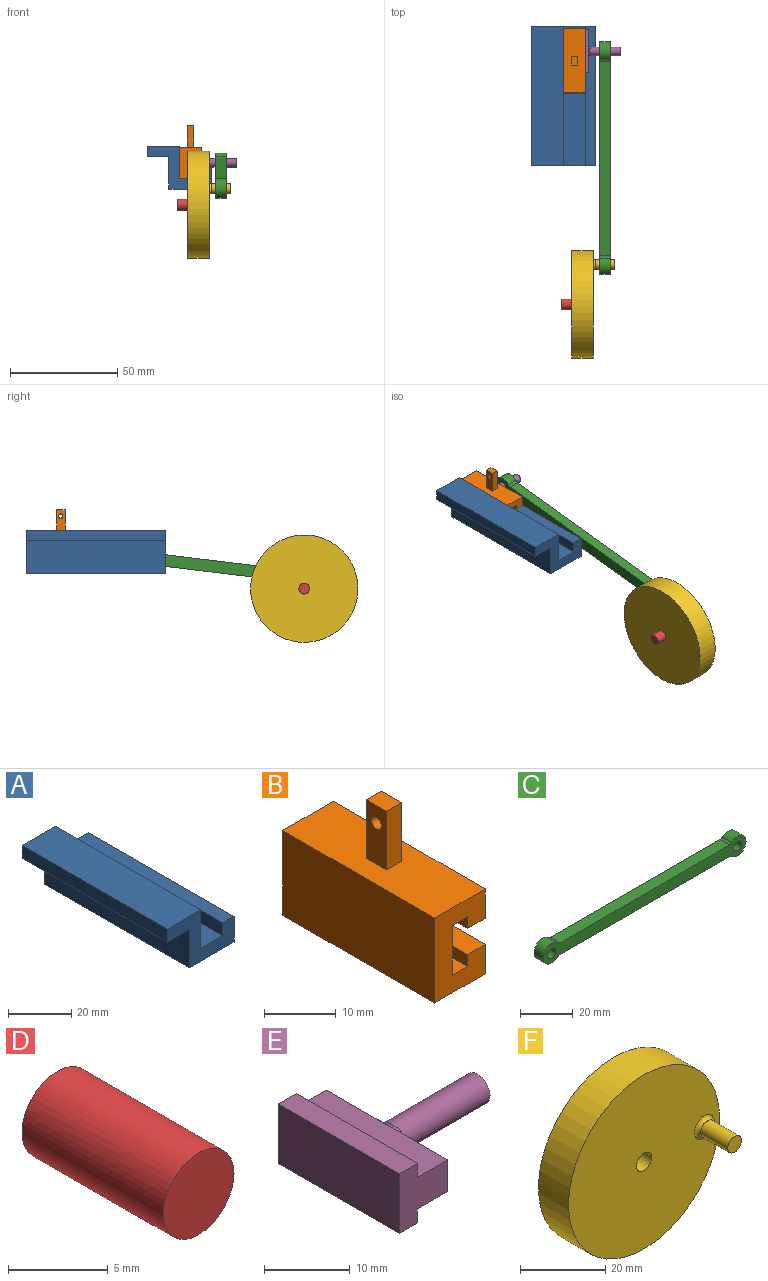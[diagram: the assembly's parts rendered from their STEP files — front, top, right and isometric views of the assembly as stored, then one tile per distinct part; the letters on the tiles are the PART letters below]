
ASSEMBLY  parts=6 mates=5
PART A: 12 faces, bbox 30x65x20 mm
  f0: plane 65x20mm, normal (0,0,-1), area 1300mm2, adj f1,f9,f10,f11
  f1: plane 65x10mm, normal (1,0,0), area 650mm2, adj f0,f2,f10,f11
  f2: plane 65x5mm, normal (0,0,1), area 325mm2, adj f1,f3,f10,f11
  f3: plane 65x5mm, normal (-1,0,0), area 325mm2, adj f2,f4,f10,f11
  f4: plane 65x10mm, normal (0,0,1), area 650mm2, adj f3,f5,f10,f11
  f5: plane 65x15mm, normal (1,0,0), area 975mm2, adj f4,f6,f10,f11
  f6: plane 65x15mm, normal (0,0,1), area 975mm2, adj f5,f7,f10,f11
  f7: plane 65x5mm, normal (-1,0,0), area 325mm2, adj f6,f8,f10,f11
  f8: plane 65x10mm, normal (0,0,-1), area 650mm2, adj f7,f9,f10,f11
  f9: plane 65x15mm, normal (-1,0,0), area 975mm2, adj f0,f8,f10,f11
  f10: plane 30x20mm, normal (0,-1,0), area 250mm2, adj f0,f1,f2,f3,f4,f5,f6,f7
  f11: plane 30x20mm, normal (0,1,0), area 250mm2, adj f0,f1,f2,f3,f4,f5,f6,f7
PART B: 20 faces, bbox 10x30x24.5 mm
  f0: plane 30x3mm, normal (0,0,1), area 90mm2, adj f1,f11,f12,f13
  f1: plane 30x8.5mm, normal (1,0,0), area 255mm2, adj f0,f2,f12,f13
  f2: plane 30x3mm, normal (0,0,-1), area 90mm2, adj f1,f3,f12,f13
  f3: plane 30x2mm, normal (-1,0,0), area 60mm2, adj f2,f4,f12,f13
  f4: plane 30x3.5mm, normal (0,0,-1), area 105mm2, adj f3,f5,f12,f13
  f5: plane 30x5mm, normal (1,0,0), area 150mm2, adj f4,f6,f12,f13
  f6: plane 30x10mm, normal (0,0,1), area 288mm2, adj f5,f7,f12,f13,f14,f15,f16,f17
  f7: plane 30x14.5mm, normal (-1,0,0), area 435mm2, adj f6,f8,f12,f13
  f8: plane 30x10mm, normal (0,0,-1), area 300mm2, adj f7,f9,f12,f13
  f9: plane 30x5mm, normal (1,0,0), area 150mm2, adj f8,f10,f12,f13
  f10: plane 30x3.5mm, normal (0,0,1), area 105mm2, adj f9,f11,f12,f13
  f11: plane 30x2mm, normal (-1,0,0), area 60mm2, adj f0,f10,f12,f13
  f12: plane 14.5x10mm, normal (0,-1,0), area 103.7mm2, adj f0,f1,f2,f3,f4,f5,f6,f7
  f13: plane 14.5x10mm, normal (0,1,0), area 103.8mm2, adj f0,f1,f2,f3,f4,f5,f6,f7
  f14: plane 10x3mm, normal (0,-1,0), area 30mm2, adj f6,f15,f17,f18
  f15: plane 10x4mm, normal (1,0,0), area 36.9mm2, adj f6,f14,f16,f18,f19
  f16: plane 10x3mm, normal (0,1,0), area 30mm2, adj f6,f15,f17,f18
  f17: plane 10x4mm, normal (-1,0,0), area 36.9mm2, adj f6,f14,f16,f18,f19
  f18: plane 4x3mm, normal (0,0,1), area 12mm2, adj f14,f15,f16,f17
  f19: cylinder r=1mm len=3mm, axis (-1,0,0), area 18.8mm2, adj f15,f17
PART C: 12 faces, bbox 109x5x9 mm
  f0: cylinder r=4.5mm len=9mm, axis (0,1,0), area 105mm2, adj f6,f7,f8,f9
  f1: plane 91.02x5mm, normal (0,0,-1), area 455.1mm2, adj f6,f7,f9,f10
  f2: cylinder r=4.5mm len=9mm, axis (0,1,0), area 105mm2, adj f6,f7,f10,f11
  f3: plane 91.02x5mm, normal (0,0,1), area 455.1mm2, adj f6,f7,f8,f11
  f4: cylinder r=2.25mm len=5mm, axis (0,1,0), area 70.7mm2, adj f6,f7
  f5: cylinder r=2mm len=5mm, axis (0,1,0), area 62.8mm2, adj f6,f7
  f6: plane 109x9mm, normal (0,-1,0), area 594mm2, adj f0,f1,f2,f3,f4,f5,f8,f9
  f7: plane 109x9mm, normal (0,1,0), area 594mm2, adj f0,f1,f2,f3,f4,f5,f8,f9
  f8: cylinder r=2mm len=5mm, axis (0,1,0), area 7.6mm2, adj f0,f3,f6,f7
  f9: cylinder r=2mm len=5mm, axis (0,1,0), area 7.6mm2, adj f0,f1,f6,f7
  f10: cylinder r=2mm len=5mm, axis (0,1,0), area 7.6mm2, adj f1,f2,f6,f7
  f11: cylinder r=2mm len=5mm, axis (0,1,0), area 7.6mm2, adj f2,f3,f6,f7
PART D: 3 faces, bbox 5x10x5 mm
  f0: cylinder r=2.5mm len=10mm, axis (0,1,0), area 157.1mm2, adj f1,f2
  f1: plane 5x5mm, normal (0,-1,0), area 19.6mm2, adj f0
  f2: plane 5x5mm, normal (0,1,0), area 19.6mm2, adj f0
PART E: 17 faces, bbox 23.1x20.1x8.6 mm
  f0: plane 8.02x4.5mm, normal (1,0,0), area 32.9mm2, adj f1,f3,f9,f14
  f1: plane 20.14x5.14mm, normal (0,0,-1), area 100mm2, adj f0,f2,f8,f9,f10,f16
  f2: plane 8.02x4.5mm, normal (1,0,0), area 32.9mm2, adj f1,f3,f10,f15
  f3: plane 20.14x5.14mm, normal (0,0,1), area 100mm2, adj f0,f2,f4,f9,f10,f13
  f4: plane 20x2mm, normal (1,0,0), area 40mm2, adj f3,f5,f9,f10
  f5: plane 20x3mm, normal (0,0,1), area 60mm2, adj f4,f6,f9,f10
  f6: plane 20x8.5mm, normal (-1,0,0), area 170mm2, adj f5,f7,f9,f10
  f7: plane 20x3mm, normal (0,0,-1), area 60mm2, adj f6,f8,f9,f10
  f8: plane 20x2mm, normal (1,0,0), area 40mm2, adj f1,f7,f9,f10
  f9: plane 8.5x8mm, normal (0,-1,0), area 48mm2, adj f0,f1,f3,f4,f5,f6,f7,f8
  f10: plane 8.5x8mm, normal (0,1,0), area 48mm2, adj f1,f2,f3,f4,f5,f6,f7,f8
  f11: cylinder r=2mm len=14.34mm, axis (-1,0,0), area 176.9mm2, adj f12,f13,f14,f15,f16
  f12: plane 4x4mm, normal (1,0,0), area 12.6mm2, adj f11
  f13: bspline ~4.24x1.13mm, area 3.2mm2, adj f3,f11,f14,f15
  f14: torus R=3mm, axis (-1,0,0), area 6.3mm2, adj f0,f11,f13,f16
  f15: torus R=3mm, axis (-1,0,0), area 6.3mm2, adj f2,f11,f13,f16
  f16: bspline ~4.24x1.13mm, area 3.2mm2, adj f1,f11,f14,f15
PART F: 7 faces, bbox 50x20x50 mm
  f0: cylinder r=2.5mm len=10mm, axis (0,1,0), area 157.1mm2, adj f2,f3
  f1: cylinder r=25mm len=50mm, axis (0,1,0), area 1570.8mm2, adj f2,f3
  f2: plane 50x50mm, normal (0,-1,0), area 1910.7mm2, adj f0,f1,f6
  f3: plane 50x50mm, normal (0,1,0), area 1943.9mm2, adj f0,f1
  f4: cylinder r=2.25mm len=9mm, axis (0,1,0), area 127.2mm2, adj f5,f6
  f5: plane 4.5x4.5mm, normal (0,-1,0), area 15.9mm2, adj f4
  f6: torus R=3.25mm, axis (0,-1,0), area 25.8mm2, adj f2,f4
PLACE A t=(19.69,58.71,-26.61)mm fixed
PLACE B t=(24.69,57.51,-14.36)mm
PLACE C rot(axis=(0.06,-0.06,1),90.2deg) t=(43.98,-52.33,-26.41)mm
PLACE D rot(axis=(-0.71,0.71,0.06),173.6deg) t=(23.48,-70.89,-33.88)mm fixed
PLACE E rot(axis=(1,0,0),180deg) t=(28.19,46.94,-14.36)mm
PLACE F rot(axis=(0.19,-0.19,0.96),92.1deg) t=(33.48,-70.89,-33.88)mm
MATE revolute E.f11 <-> C.f2  axis (-1,0,0) through (43.98,46.94,-14.36)mm
MATE slider A.f10 <-> B.f12  axis (0,-1,0) through (29.69,-6.29,-21.61)mm
MATE slider E.f9 <-> B.f13  axis (0,1,0) through (28.19,56.94,-14.36)mm
MATE revolute F.f4 <-> C.f0  axis (-1,0,0) through (43.98,-52.33,-26.41)mm
MATE revolute D.f0 <-> F.f0  axis (-1,0,0) through (28.48,-70.89,-33.88)mm
